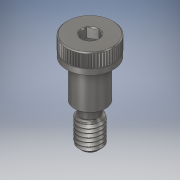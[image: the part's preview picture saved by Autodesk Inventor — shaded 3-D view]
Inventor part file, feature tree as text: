
AUTODESK INVENTOR PART (.ipt)
format: ipt  version: 2017 (Build 210142000, 142)  size: 602,624 bytes
history: native  units: in
note: dims shown in document units (in); Inventor stores cm internally (conversion verified against a paired STEP export)
features: chamfer x1
ambient origin geometry x8: Origin, YZ Plane, XZ Plane, XY Plane, X Axis, Y Axis, Z Axis, Center Point
bodies: Solid1 (feature_tree)
feature tree (1):
  chamfer  "Chamfer3"  [1 undecoded]
note: 1 required parameter value undecoded (feature->parameter linkage not recoverable at this tier; creation-order binding heuristic only, values carry confidence <= 0.55)
